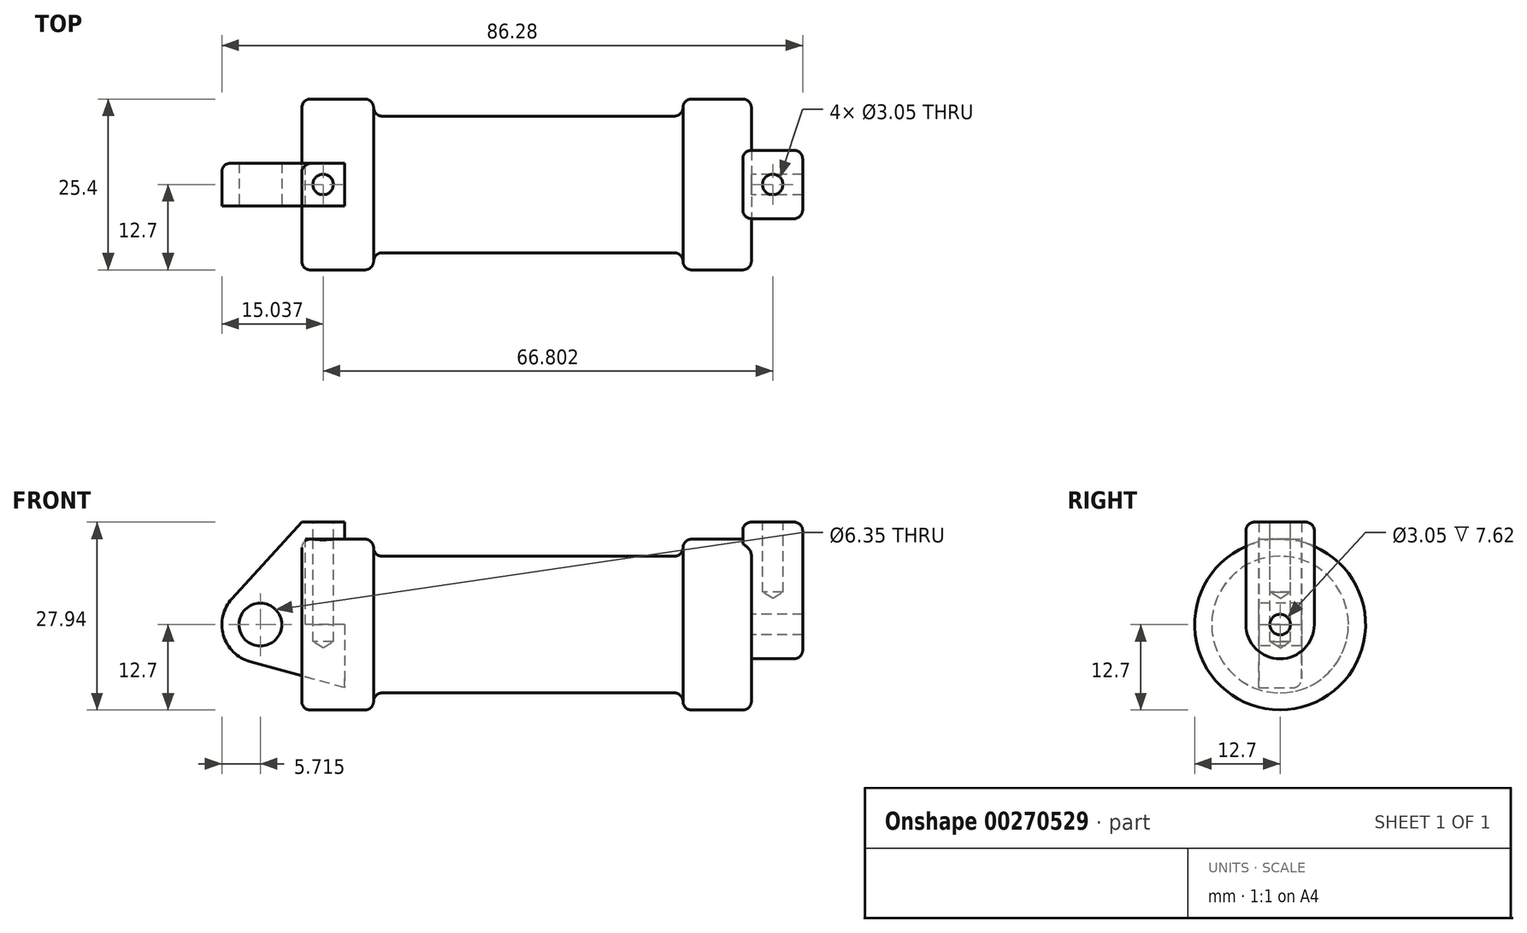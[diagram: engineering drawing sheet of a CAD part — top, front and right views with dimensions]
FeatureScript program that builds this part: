
annotation { "Feature Type Name" : "Feature", "Feature Type Description" : "" }
export const myFeature = defineFeature(function(context is Context, id is Id, definition is map)
    precondition{}
    {
        {
            var Q0;
            Q0=qCreatedBy(makeId("Front.planeOp"),FACE);
            var sketch = newSketch(context, id + "F0", { "sketchPlane" : qUnion([Q0])});
            skLineSegment(sketch, "E0", {"start": v(0, 0) * mm, "end": v(0, 12.7) * mm});
            skLineSegment(sketch, "E1", {"start": v(0, 12.7) * mm, "end": v(10.16, 12.7) * mm});
            skLineSegment(sketch, "E2", {"start": v(10.16, 12.7) * mm, "end": v(10.16, 10.16) * mm});
            skLineSegment(sketch, "E3", {"start": v(10.16, 10.16) * mm, "end": v(56.13, 10.16) * mm});
            skLineSegment(sketch, "E4", {"start": v(56.13, 10.16) * mm, "end": v(56.13, 12.7) * mm});
            skLineSegment(sketch, "E5", {"start": v(56.13, 12.7) * mm, "end": v(66.3, 12.7) * mm});
            skLineSegment(sketch, "E6", {"start": v(66.3, 12.7) * mm, "end": v(66.3, 0) * mm});
            skLineSegment(sketch, "E7", {"start": v(66.3, 0) * mm, "end": v(0, 0) * mm});
            skLineSegment(sketch, "E8", {"start": v(5.84, 15.24) * mm, "end": v(-0.5, 15.24) * mm});
            skLineSegment(sketch, "E9", {"start": v(-0.5, 15.24) * mm, "end": v(-10.88, 3.85) * mm});
            skLineSegment(sketch, "E10", {"start": v(0, 0) * mm, "end": v(-6.65, 0) * mm});
            skCircle(sketch, "E11", {"center": v(-6.65, 0) * mm, "radius": 5.72 * mm});
            skCircle(sketch, "E12", {"center": v(-6.65, 0) * mm, "radius": 3.18 * mm});
            skLineSegment(sketch, "E13", {"start": v(5.84, 15.24) * mm, "end": v(5.84, -9.4) * mm});
            skLineSegment(sketch, "E14", {"start": v(5.84, -9.4) * mm, "end": v(-8.18, -5.5) * mm});
            skSolve(sketch);
        }
        {
            var Q0;
            {var subQ0=sQuery(id+"F0.wireOp",EDGE,"E2");Q0=makeQuery(id+"F0.imprint","IMPRINT",FACE,{"disambiguationData":[TD([[makeQuery(id+"F0.imprint","IMPRINT",EDGE,{"derivedFrom":subQ0}),-1.0]])]});}
            var Q1;
            Q1=sQuery(id+"F0.wireOp",EDGE,"E7");
            revolve(context, id + "F1", {"entities" : qUnion([Q0]), "axis" : qUnion([Q1]), "revolveType" : RevolveType.FULL});
        }
        {
            var Q0;
            Q0=makeQuery(id+"F1.opRevolve","SWEPT_FACE",FACE,{"disambiguationData":[OSD([sQuery(id+"F0.wireOp",EDGE,"E13")])]});
            var Q1;
            Q1=sQuery(id+"F0.wireOp",VERTEX,"E1.start");
            extrude(context, id + "F2", {"entities" : qUnion([Q0]), "operationType" : NewBodyOperationType.ADD, "endBoundEntityVertex" : qUnion([Q1]), "depth" : 6.35 * mm});
        }
        {
            var Q0;
            {var subQ3=sQuery(id+"F0.wireOp",EDGE,"E0");Q0=makeQuery(id+"F0.imprint","IMPRINT",FACE,{"disambiguationData":[TD([[makeQuery(id+"F0.imprint","IMPRINT",EDGE,{"derivedFrom":subQ3}),1.0]])]});}
            var Q1;
            {var subQ0=sQuery(id+"F0.wireOp",EDGE,"E12");Q1=makeQuery(id+"F0.imprint","IMPRINT",FACE,{"disambiguationData":[TD([[makeQuery(id+"F0.imprint","IMPRINT",EDGE,{"derivedFrom":subQ0}),1.0]])]});}
            var Q2;
            {var subQ4=sQuery(id+"F0.wireOp",EDGE,"E12");Q2=makeQuery(id+"F0.imprint","IMPRINT",FACE,{"disambiguationData":[TD([[makeQuery(id+"F0.imprint","IMPRINT",EDGE,{"derivedFrom":subQ4}),-1.0]])]});}
            var Q3;
            {var subQ0=sQuery(id+"F0.wireOp",EDGE,"E14");Q3=makeQuery(id+"F0.imprint","IMPRINT",FACE,{"disambiguationData":[TD([[makeQuery(id+"F0.imprint","IMPRINT",EDGE,{"derivedFrom":subQ0}),-1.0]])]});}
            var Q4;
            Q4 = qSketchRegion(id + "F4", true);
            var Q5;
            Q5=sQuery(id+"F0.wireOp",EDGE,"E8");
            var Q6;
            Q6=sQuery(id+"F0.wireOp",EDGE,"E9");
            var Q7;
            Q7=sQuery(id+"F0.wireOp",EDGE,"E1");
            var Q8;
            Q8=sQuery(id+"F0.wireOp",EDGE,"E13");
            var Q9;
            Q9=sQuery(id+"F0.wireOp",EDGE,"E11");
            var Q10;
            Q10=sQuery(id+"F0.wireOp",EDGE,"E12");
            extrude(context, id + "F3", {"entities" : qUnion([Q0, Q1, Q2, Q3, Q4]), "surfaceEntities" : qUnion([Q5, Q6, Q7, Q8, Q9, Q10]), "endBound" : BoundingType.SYMMETRIC, "depth" : 6.35 * mm});
        }
        {
            var Q0;
            Q0=makeQuery(id+"F1.opRevolve","SWEPT_FACE",FACE,{"disambiguationData":[OSD([sQuery(id+"F0.wireOp",EDGE,"E6")])]});
            var sketch = newSketch(context, id + "F4", { "sketchPlane" : qUnion([Q0])});
            skCircle(sketch, "E15", {"center": v(0, 0) * mm, "radius": 5.08 * mm});
            skCircle(sketch, "E16", {"center": v(0, 0) * mm, "radius": 1.52 * mm});
            skLineSegment(sketch, "E17", {"start": v(5.08, 0) * mm, "end": v(5.08, 15.24) * mm});
            skLineSegment(sketch, "E18", {"start": v(-5.08, 0) * mm, "end": v(-5.08, 15.24) * mm});
            skLineSegment(sketch, "E19", {"start": v(-5.08, 15.24) * mm, "end": v(5.08, 15.24) * mm});
            skSolve(sketch);
        }
        {
            var Q0;
            Q0 = qSketchRegion(id + "F4", true);
            extrude(context, id + "F5", {"entities" : qUnion([Q0]), "operationType" : NewBodyOperationType.ADD, "depth" : 7.62 * mm});
        }
        {
            var Q0;
            Q0 = qSketchRegion(id + "F4", true);
            extrude(context, id + "F6", {"entities" : qUnion([Q0]), "operationType" : NewBodyOperationType.ADD, "oppositeDirection" : true, "depth" : 1.27 * mm});
        }
        {
            var Q0;
            Q0=sQuery(id+"F0.wireOp",VERTEX,"E10.end");
            var Q1;
            Q1=makeQuery(id+"F3.opExtrude","SWEPT_BODY",BODY,{"disambiguationData":[OSD([sQuery(id+"F0.wireOp",EDGE,"E0"),sQuery(id+"F0.wireOp",EDGE,"E1"),sQuery(id+"F0.wireOp",EDGE,"E7"),sQuery(id+"F0.wireOp",EDGE,"E8"),sQuery(id+"F0.wireOp",EDGE,"E9"),sQuery(id+"F0.wireOp",EDGE,"E11"),sQuery(id+"F0.wireOp",EDGE,"E13"),sQuery(id+"F0.wireOp",EDGE,"E14")])]});
            hole(context, id + "F7", {"style" : HoleStyle.SIMPLE, "endStyle" : HoleEndStyle.THROUGH, "holeDiameter" : 6.35 * mm, "tappedDepth" : 12.7 * mm, "tapClearance" : 3, "locations" : qUnion([Q0]), "scope" : qUnion([Q1])});
        }
        {
            var Q0;
            Q0=sQuery(id+"F0.wireOp",VERTEX,"E10.end");
            var Q1;
            Q1=makeQuery(id+"F3.opExtrude","SWEPT_BODY",BODY,{"disambiguationData":[OSD([sQuery(id+"F0.wireOp",EDGE,"E0"),sQuery(id+"F0.wireOp",EDGE,"E1"),sQuery(id+"F0.wireOp",EDGE,"E7"),sQuery(id+"F0.wireOp",EDGE,"E8"),sQuery(id+"F0.wireOp",EDGE,"E9"),sQuery(id+"F0.wireOp",EDGE,"E11"),sQuery(id+"F0.wireOp",EDGE,"E13"),sQuery(id+"F0.wireOp",EDGE,"E14")])]});
            hole(context, id + "F8", {"style" : HoleStyle.SIMPLE, "endStyle" : HoleEndStyle.THROUGH, "oppositeDirection" : true, "holeDiameter" : 6.35 * mm, "tappedDepth" : 12.7 * mm, "tapClearance" : 3, "locations" : qUnion([Q0]), "scope" : qUnion([Q1])});
        }
        {
            var Q0;
            Q0=sQuery(id+"F0.wireOp",EDGE,"E8");
            cPoint(context, id + "F9", {"entities" : qUnion([Q0]), "parameter" : 0.5});
        }
        {
            var Q0;
            Q0 = qCreatedBy(id + "F9" ,VERTEX);
            var Q1;
            Q1=makeQuery(id+"F3.opExtrude","SWEPT_FACE",FACE,{"disambiguationData":[OSD([sQuery(id+"F0.wireOp",EDGE,"E8")])]});
            cPlane(context, id + "F10", {"entities" : qUnion([Q0, Q1]), "cplaneType" : CPlaneType.PLANE_POINT, "offset" : 25.4 * mm, "oppositeDirection" : true, "width" : 152.4 * mm, "height" : 152.4 * mm});
        }
        {
            var Q0;
            Q0=qCreatedBy(id+"F10.planeOp",FACE);
            var sketch = newSketch(context, id + "F11", { "sketchPlane" : qUnion([Q0])});
            skCircle(sketch, "E20", {"center": v(2.67, 0) * mm, "radius": 1.52 * mm});
            skSolve(sketch);
        }
        {
            var Q0;
            Q0=sQuery(id+"F11.wireOp",VERTEX,"E20.center");
            var Q1;
            Q1=makeQuery(id+"F1.opRevolve","SWEPT_BODY",BODY,{"disambiguationData":[OSD([sQuery(id+"F0.wireOp",EDGE,"E1"),sQuery(id+"F0.wireOp",EDGE,"E2"),sQuery(id+"F0.wireOp",EDGE,"E3"),sQuery(id+"F0.wireOp",EDGE,"E4"),sQuery(id+"F0.wireOp",EDGE,"E5"),sQuery(id+"F0.wireOp",EDGE,"E6"),sQuery(id+"F0.wireOp",EDGE,"E7"),sQuery(id+"F0.wireOp",EDGE,"E13")])]});
            var Q2;
            Q2=makeQuery(id+"F3.opExtrude","SWEPT_BODY",BODY,{"disambiguationData":[OSD([sQuery(id+"F0.wireOp",EDGE,"E0"),sQuery(id+"F0.wireOp",EDGE,"E1"),sQuery(id+"F0.wireOp",EDGE,"E7"),sQuery(id+"F0.wireOp",EDGE,"E8"),sQuery(id+"F0.wireOp",EDGE,"E9"),sQuery(id+"F0.wireOp",EDGE,"E11"),sQuery(id+"F0.wireOp",EDGE,"E13"),sQuery(id+"F0.wireOp",EDGE,"E14")])]});
            hole(context, id + "F12", {"style" : HoleStyle.SIMPLE, "endStyle" : HoleEndStyle.BLIND, "holeDiameter" : 3.05 * mm, "holeDepth" : 17.78 * mm, "tappedDepth" : 12.7 * mm, "tapClearance" : 3, "locations" : qUnion([Q0]), "scope" : qUnion([Q1, Q2])});
        }
        {
            var Q0;
            {var subQ0=sQuery(id+"F4.wireOp",EDGE,"E19");Q0=makeQuery(id+"F6.boolean.opBoolean","MERGE",FACE,{"derivedFrom":[makeQuery(id+"F5.opExtrude","SWEPT_FACE",FACE,{"disambiguationData":[OSD([subQ0])]}),makeQuery(id+"F6.opExtrude","SWEPT_FACE",FACE,{"disambiguationData":[OSD([subQ0])]})]});}
            var sketch = newSketch(context, id + "F13", { "sketchPlane" : qUnion([Q0])});
            skCircle(sketch, "E21", {"center": v(69.47, 0) * mm, "radius": 1.52 * mm});
            skSolve(sketch);
        }
        {
            var Q0;
            Q0=sQuery(id+"F13.wireOp",VERTEX,"E21.center");
            var Q1;
            Q1=makeQuery(id+"F1.opRevolve","SWEPT_BODY",BODY,{"disambiguationData":[OSD([sQuery(id+"F0.wireOp",EDGE,"E1"),sQuery(id+"F0.wireOp",EDGE,"E2"),sQuery(id+"F0.wireOp",EDGE,"E3"),sQuery(id+"F0.wireOp",EDGE,"E4"),sQuery(id+"F0.wireOp",EDGE,"E5"),sQuery(id+"F0.wireOp",EDGE,"E6"),sQuery(id+"F0.wireOp",EDGE,"E7"),sQuery(id+"F0.wireOp",EDGE,"E13")])]});
            hole(context, id + "F14", {"style" : HoleStyle.SIMPLE, "endStyle" : HoleEndStyle.BLIND, "holeDiameter" : 3.05 * mm, "holeDepth" : 10.4 * mm, "tappedDepth" : 12.7 * mm, "tapClearance" : 3, "locations" : qUnion([Q0]), "scope" : qUnion([Q1])});
        }
        {
            var Q0;
            Q0=makeQuery(id+"F1.opRevolve","SWEPT_EDGE",EDGE,{"disambiguationData":[OSD([sQuery(id+"F0.wireOp",EDGE,"E1"),sQuery(id+"F0.wireOp",EDGE,"E2")])]});
            var Q1;
            Q1=makeQuery(id+"F1.opRevolve","SWEPT_FACE",FACE,{"disambiguationData":[OSD([sQuery(id+"F0.wireOp",EDGE,"E3")])]});
            fillet(context, id + "F15", {"entities" : qUnion([Q0, Q1]), "radius" : 1.27 * mm, "tangentPropagation" : true, "allowEdgeOverflow" : false});
        }
        {
            var Q0;
            Q0=makeQuery(id+"F1.opRevolve","SWEPT_EDGE",EDGE,{"disambiguationData":[OSD([sQuery(id+"F0.wireOp",EDGE,"E4"),sQuery(id+"F0.wireOp",EDGE,"E5")])]});
            fillet(context, id + "F16", {"entities" : qUnion([Q0]), "radius" : 1.27 * mm, "tangentPropagation" : true, "allowEdgeOverflow" : false});
        }
        {
            var Q0;
            {var subQ0=sQuery(id+"F4.wireOp",EDGE,"E19");var subQ1=sQuery(id+"F4.wireOp",EDGE,"E18");Q0=makeQuery(id+"F6.boolean.opBoolean","MERGE",EDGE,{"derivedFrom":[makeQuery(id+"F5.opExtrude","SWEPT_EDGE",EDGE,{"disambiguationData":[OSD([subQ1,subQ0])]}),makeQuery(id+"F6.opExtrude","SWEPT_EDGE",EDGE,{"disambiguationData":[OSD([subQ1,subQ0])]})]});}
            var Q1;
            {var subQ0=sQuery(id+"F0.wireOp",EDGE,"E5");var subQ1=sQuery(id+"F0.wireOp",EDGE,"E6");Q1=makeQuery(id+"F5.boolean.opBoolean","SPLIT",EDGE,{"disambiguationData":[topologyDisambiguationEdgeConnected([makeQuery(id+"F1.opRevolve","SWEPT_FACE",FACE,{"disambiguationData":[OSD([subQ1])]})])],"derivedFrom":makeQuery(id+"F1.opRevolve","SWEPT_EDGE",EDGE,{"disambiguationData":[OSD([subQ0,subQ1])]})});}
            fillet(context, id + "F17", {"entities" : qUnion([Q0, Q1]), "radius" : 1.27 * mm, "tangentPropagation" : true, "allowEdgeOverflow" : false});
        }
        {
            var Q0;
            Q0=makeQuery(id+"F5.opExtrude","CAP_EDGE",EDGE,{"disambiguationData":[OSD([sQuery(id+"F4.wireOp",EDGE,"E18")])],"isStart":false});
            var Q1;
            {var subQ0=sQuery(id+"F4.wireOp",EDGE,"E19");var subQ1=sQuery(id+"F4.wireOp",EDGE,"E17");Q1=makeQuery(id+"F6.boolean.opBoolean","MERGE",EDGE,{"derivedFrom":[makeQuery(id+"F5.opExtrude","SWEPT_EDGE",EDGE,{"disambiguationData":[OSD([subQ1,subQ0])]}),makeQuery(id+"F6.opExtrude","SWEPT_EDGE",EDGE,{"disambiguationData":[OSD([subQ1,subQ0])]})]});}
            fillet(context, id + "F18", {"entities" : qUnion([Q0, Q1]), "radius" : 1.27 * mm, "tangentPropagation" : true, "allowEdgeOverflow" : false});
        }
        {
            var Q0;
            Q0=makeQuery(id+"F6.opExtrude","CAP_EDGE",EDGE,{"disambiguationData":[OSD([sQuery(id+"F4.wireOp",EDGE,"E19")])],"isStart":false});
            fillet(context, id + "F19", {"entities" : qUnion([Q0]), "radius" : 1.27 * mm, "tangentPropagation" : true, "allowEdgeOverflow" : false});
        }
        {
            var Q0;
            Q0=makeQuery(id+"F2.opExtrude","CAP_EDGE",EDGE,{"disambiguationData":[OSD([sQuery(id+"F0.wireOp",EDGE,"E1"),sQuery(id+"F0.wireOp",EDGE,"E13")])],"isStart":false});
            var Q1;
            Q1=makeQuery(id+"F3.opExtrude","CAP_EDGE",EDGE,{"disambiguationData":[OSD([sQuery(id+"F0.wireOp",EDGE,"E9")])],"isStart":true});
            fillet(context, id + "F20", {"entities" : qUnion([Q0, Q1]), "radius" : 1.27 * mm, "tangentPropagation" : true, "allowEdgeOverflow" : false});
        }
    });
